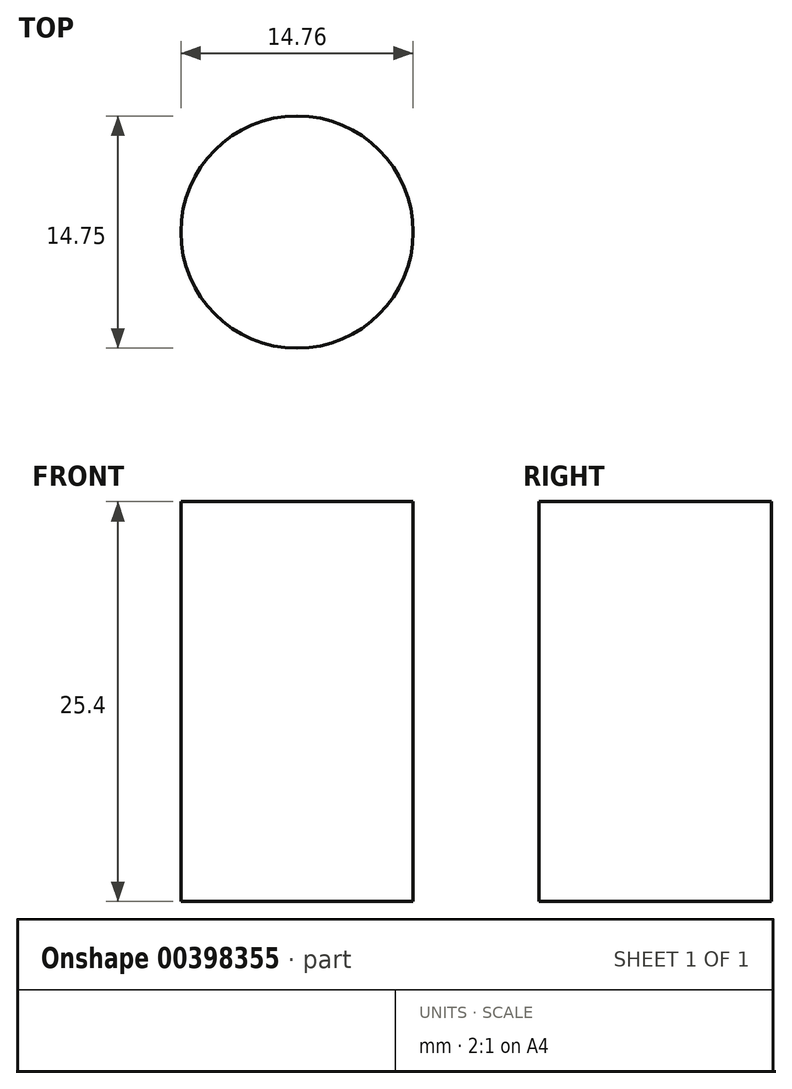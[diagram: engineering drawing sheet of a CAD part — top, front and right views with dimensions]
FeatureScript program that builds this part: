
annotation { "Feature Type Name" : "Feature", "Feature Type Description" : "" }
export const myFeature = defineFeature(function(context is Context, id is Id, definition is map)
    precondition{}
    {
        {
            var Q0;
            Q0=qCreatedBy(makeId("Top.planeOp"),FACE);
            var sketch = newSketch(context, id + "F0", { "sketchPlane" : qUnion([Q0])});
            skCircle(sketch, "E0", {"center": v(0, 0.18) * mm, "radius": 7.38 * mm});
            skSolve(sketch);
        }
        {
            var Q0;
            Q0=makeQuery(id+"F0.imprint","IMPRINT",FACE,{"disambiguationData":[TD([[makeQuery(id+"F0.imprint","IMPRINT",EDGE,{"derivedFrom":sQuery(id+"F0.wireOp",EDGE,"E0")}),1.0]])]});
            extrude(context, id + "F1", {"entities" : qUnion([Q0]), "depth" : 25.4 * mm});
        }
    });
